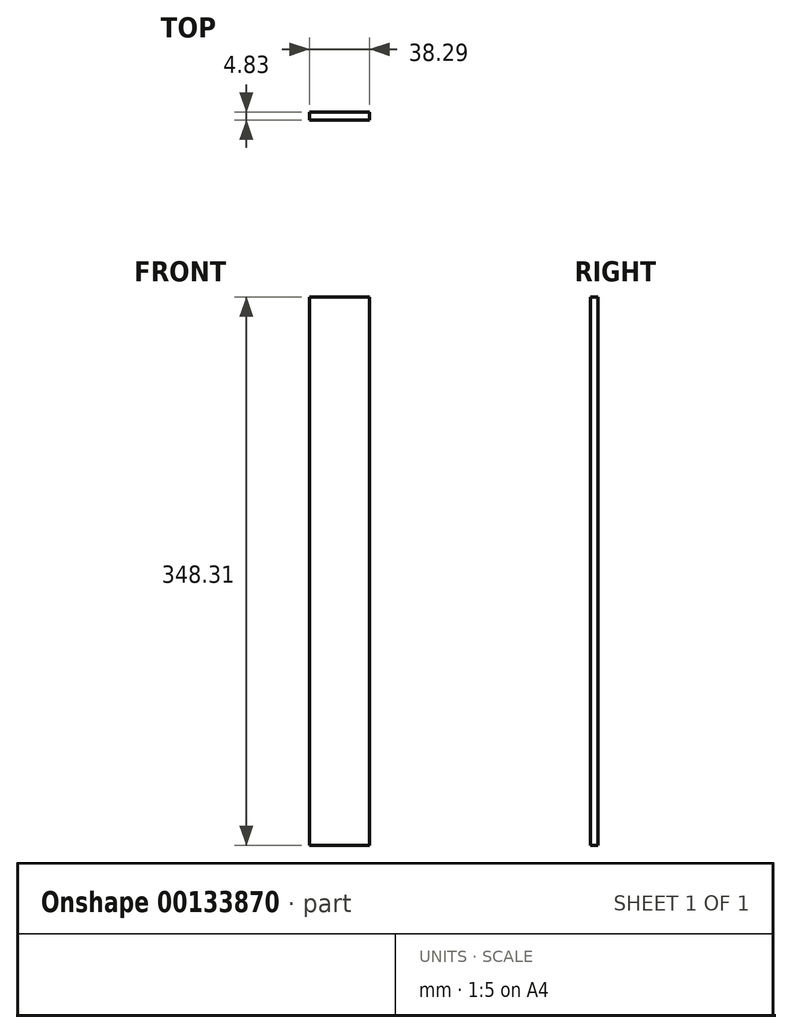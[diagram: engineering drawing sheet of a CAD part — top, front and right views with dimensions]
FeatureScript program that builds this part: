
annotation { "Feature Type Name" : "Feature", "Feature Type Description" : "" }
export const myFeature = defineFeature(function(context is Context, id is Id, definition is map)
    precondition{}
    {
        {
            var Q0;
            Q0=qCreatedBy(makeId("Front.planeOp"),FACE);
            var sketch = newSketch(context, id + "F0", { "sketchPlane" : qUnion([Q0])});
            skLineSegment(sketch, "E0.bottom", {"start": v(-38.3, 106.2) * mm, "end": v(0, 106.2) * mm});
            skLineSegment(sketch, "E0.top", {"start": v(-38.3, -242.12) * mm, "end": v(0, -242.12) * mm});
            skLineSegment(sketch, "E0.left", {"start": v(-38.3, 106.2) * mm, "end": v(-38.3, -242.12) * mm});
            skLineSegment(sketch, "E0.right", {"start": v(0, 106.2) * mm, "end": v(0, -242.12) * mm});
            skSolve(sketch);
        }
        {
            var Q0;
            Q0=makeQuery(id+"F0.imprint","IMPRINT",FACE,{"disambiguationData":[TD([[makeQuery(id+"F0.imprint","IMPRINT",EDGE,{"derivedFrom":sQuery(id+"F0.wireOp",EDGE,"E0.bottom")}),-1.0]])]});
            extrude(context, id + "F1", {"entities" : qUnion([Q0]), "depth" : 4.83 * mm});
        }
    });
